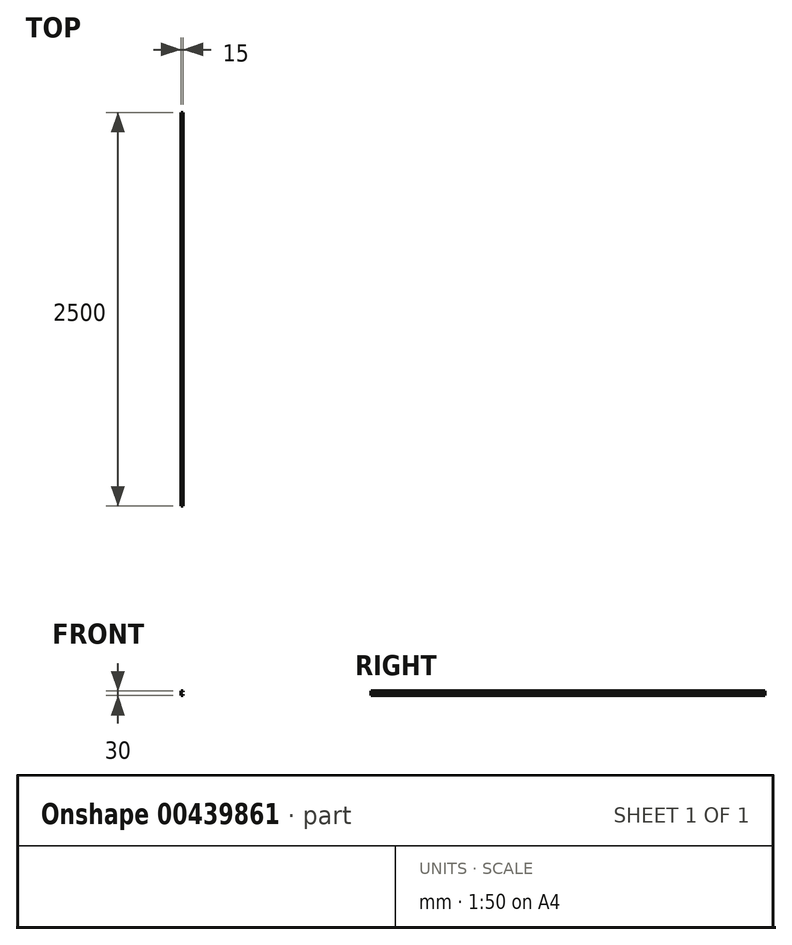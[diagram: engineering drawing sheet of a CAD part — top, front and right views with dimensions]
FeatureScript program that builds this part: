
annotation { "Feature Type Name" : "Feature", "Feature Type Description" : "" }
export const myFeature = defineFeature(function(context is Context, id is Id, definition is map)
    precondition{}
    {
        {
            var Q0;
            Q0=qCreatedBy(makeId("Front.planeOp"),FACE);
            var sketch = newSketch(context, id + "F0", { "sketchPlane" : qUnion([Q0])});
            skLineSegment(sketch, "E0", {"start": v(0, 0) * mm, "end": v(0, 30) * mm});
            skLineSegment(sketch, "E1", {"start": v(0, 30) * mm, "end": v(15, 30) * mm});
            skLineSegment(sketch, "E2", {"start": v(15, 30) * mm, "end": v(15, 22.5) * mm});
            skLineSegment(sketch, "E3", {"start": v(0, 0) * mm, "end": v(15, 0) * mm});
            skLineSegment(sketch, "E4", {"start": v(15, 0) * mm, "end": v(15, 7.5) * mm});
            skLineSegment(sketch, "E5.0", {"start": v(13.5, 28.5) * mm, "end": v(13.5, 22.5) * mm});
            skLineSegment(sketch, "E5.1", {"start": v(13.5, 1.5) * mm, "end": v(13.5, 7.5) * mm});
            skLineSegment(sketch, "E5.2", {"start": v(1.5, 1.5) * mm, "end": v(13.5, 1.5) * mm});
            skLineSegment(sketch, "E5.3", {"start": v(1.5, 1.5) * mm, "end": v(1.5, 28.5) * mm});
            skLineSegment(sketch, "E5.4", {"start": v(1.5, 28.5) * mm, "end": v(13.5, 28.5) * mm});
            skLineSegment(sketch, "E6", {"start": v(13.5, 22.5) * mm, "end": v(15, 22.5) * mm});
            skLineSegment(sketch, "E7", {"start": v(13.5, 7.5) * mm, "end": v(15, 7.5) * mm});
            skSolve(sketch);
        }
        {
            var Q0;
            Q0 = qSketchRegion(id + "F0", true);
            extrude(context, id + "F1", {"entities" : qUnion([Q0]), "depth" : 2500 * mm});
        }
    });
